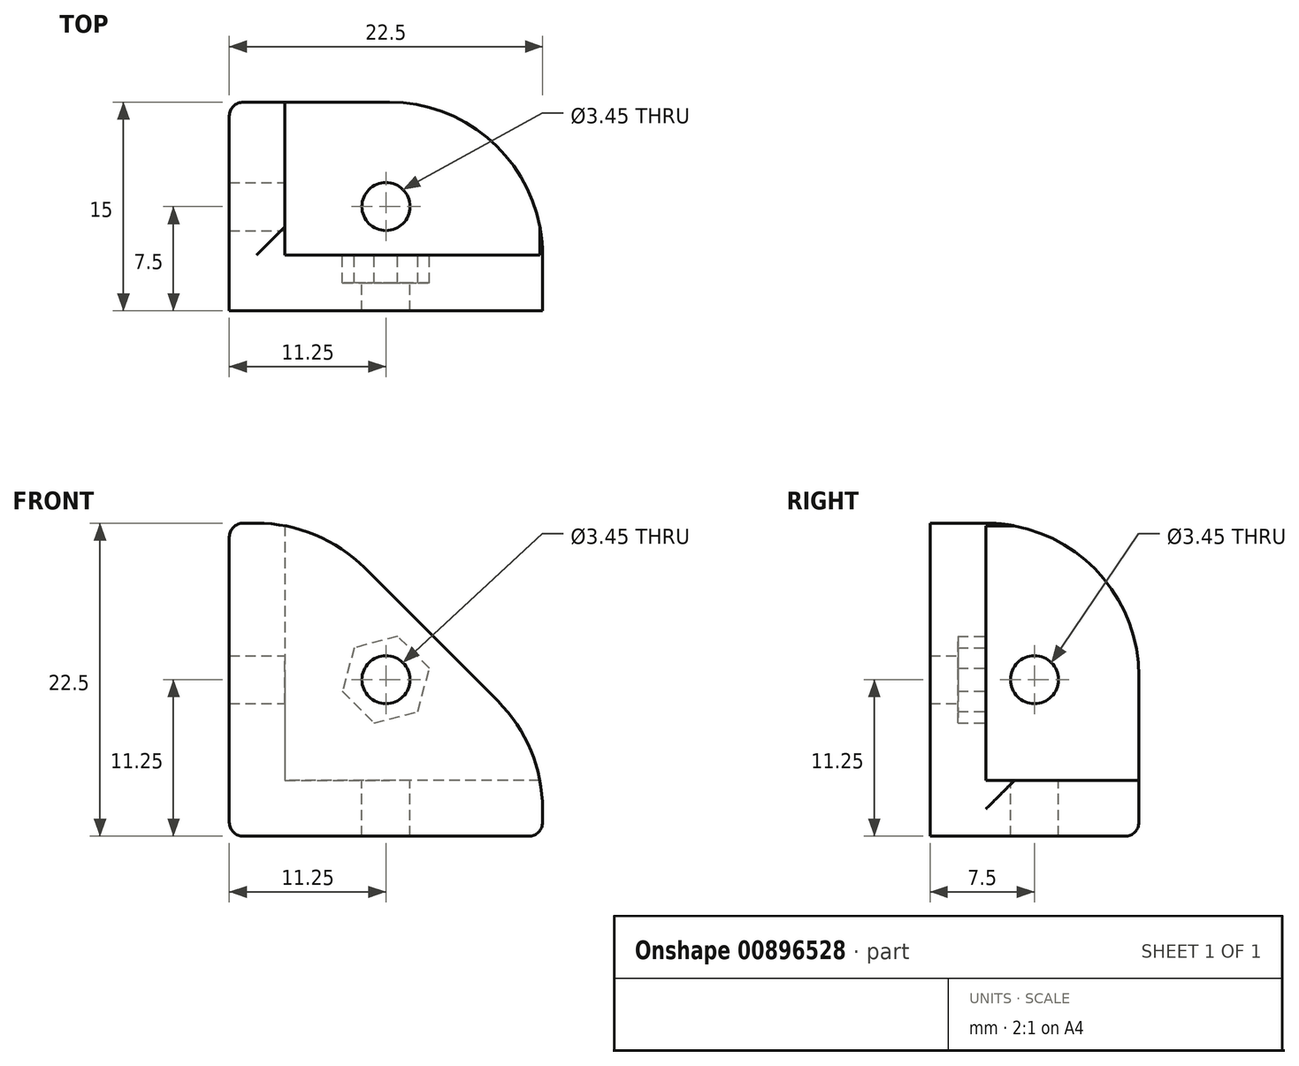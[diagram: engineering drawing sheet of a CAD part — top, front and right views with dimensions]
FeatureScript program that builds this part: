
annotation { "Feature Type Name" : "Feature", "Feature Type Description" : "" }
export const myFeature = defineFeature(function(context is Context, id is Id, definition is map)
    precondition{}
    {
        {
            assignVariable(context, id + "F0", {"variableType" : VariableType.LENGTH, "name" : "BeamWidth", "lengthValue" : 15 * mm});
        }
        {
            var Q0;
            Q0=qCreatedBy(makeId("Top.planeOp"),FACE);
            var sketch = newSketch(context, id + "F1", { "sketchPlane" : qUnion([Q0])});
            skLineSegment(sketch, "E0.bottom", {"start": v(0, 0) * mm, "end": v(22.5, 0) * mm});
            skLineSegment(sketch, "E0.top", {"start": v(0, 15) * mm, "end": v(22.5, 15) * mm});
            skLineSegment(sketch, "E0.left", {"start": v(0, 0) * mm, "end": v(0, 15) * mm});
            skLineSegment(sketch, "E0.right", {"start": v(22.5, 0) * mm, "end": v(22.5, 15) * mm});
            skSolve(sketch);
        }
        {
            var Q0;
            Q0 = qSketchRegion(id + "F1", true);
            extrude(context, id + "F2", {"entities" : qUnion([Q0]), "depth" : 4 * mm, "offsetDistance" : 25 * mm});
        }
        {
            var Q0;
            Q0=makeQuery(id+"F2.opExtrude","CAP_FACE",FACE,{"disambiguationData":[OSD([sQuery(id+"F1.wireOp",EDGE,"E0.bottom"),sQuery(id+"F1.wireOp",EDGE,"E0.top"),sQuery(id+"F1.wireOp",EDGE,"E0.left"),sQuery(id+"F1.wireOp",EDGE,"E0.right")])],"isStart":false});
            var sketch = newSketch(context, id + "F3", { "sketchPlane" : qUnion([Q0])});
            skLineSegment(sketch, "E1", {"start": v(0, 15) * mm, "end": v(0, 0) * mm});
            skLineSegment(sketch, "E2", {"start": v(0, 0) * mm, "end": v(22.5, 0) * mm});
            skLineSegment(sketch, "E3", {"start": v(22.5, 0) * mm, "end": v(22.5, 4) * mm});
            skLineSegment(sketch, "E4", {"start": v(22.5, 4) * mm, "end": v(4, 4) * mm});
            skLineSegment(sketch, "E5", {"start": v(4, 4) * mm, "end": v(4, 15) * mm});
            skLineSegment(sketch, "E6", {"start": v(4, 15) * mm, "end": v(0, 15) * mm});
            skSolve(sketch);
        }
        {
            var Q0;
            Q0 = qSketchRegion(id + "F3", true);
            extrude(context, id + "F4", {"entities" : qUnion([Q0]), "operationType" : NewBodyOperationType.ADD, "depth" : ((getVariable(context, 'BeamWidth') * 1.5) - 4 * mm), "offsetDistance" : 25 * mm});
        }
        {
            var Q0;
            Q0=makeQuery(id+"F2.opExtrude","CAP_FACE",FACE,{"disambiguationData":[OSD([sQuery(id+"F1.wireOp",EDGE,"E0.bottom"),sQuery(id+"F1.wireOp",EDGE,"E0.top"),sQuery(id+"F1.wireOp",EDGE,"E0.left"),sQuery(id+"F1.wireOp",EDGE,"E0.right")])],"isStart":false});
            var sketch = newSketch(context, id + "F5", { "sketchPlane" : qUnion([Q0])});
            skLineSegment(sketch, "E7.0", {"start": v(0, 0) * mm, "end": v(0, 15) * mm});
            skLineSegment(sketch, "E8.0", {"start": v(0, 0) * mm, "end": v(22.5, 0) * mm});
            skCircle(sketch, "E9", {"center": v(11.25, 7.5) * mm, "radius": 1.73 * mm});
            skLineSegment(sketch, "E10", {"start": v(0, 7.5) * mm, "end": v(11.25, 7.5) * mm, "construction": true});
            skLineSegment(sketch, "E11", {"start": v(11.25, 0) * mm, "end": v(11.25, 7.5) * mm, "construction": true});
            skCircle(sketch, "E12", {"center": v(11.25, 7.5) * mm, "radius": 3.5 * mm});
            skSolve(sketch);
        }
        {
            var Q0;
            Q0=makeQuery(id+"F5.imprint","IMPRINT",FACE,{"disambiguationData":[TD([[makeQuery(id+"F5.imprint","IMPRINT",EDGE,{"derivedFrom":sQuery(id+"F5.wireOp",EDGE,"E9")}),1.0]])]});
            extrude(context, id + "F6", {"entities" : qUnion([Q0]), "operationType" : NewBodyOperationType.REMOVE, "endBound" : BoundingType.UP_TO_NEXT, "oppositeDirection" : true, "depth" : 25 * mm, "offsetDistance" : 25 * mm});
        }
        {
            var Q0;
            Q0=makeQuery(id+"F4.opExtrude","SWEPT_FACE",FACE,{"disambiguationData":[OSD([sQuery(id+"F3.wireOp",EDGE,"E5")])]});
            var sketch = newSketch(context, id + "F7", { "sketchPlane" : qUnion([Q0])});
            skCircle(sketch, "E13", {"center": v(7.5, 11.25) * mm, "radius": 1.73 * mm});
            skLineSegment(sketch, "E14.0", {"start": v(0, 0) * mm, "end": v(15, 0) * mm});
            skLineSegment(sketch, "E15", {"start": v(7.5, 0) * mm, "end": v(7.5, 11.25) * mm, "construction": true});
            skLineSegment(sketch, "E16", {"start": v(0, 0) * mm, "end": v(0, 22.5) * mm, "construction": true});
            skLineSegment(sketch, "E17", {"start": v(7.5, 11.25) * mm, "end": v(0, 11.25) * mm, "construction": true});
            skCircle(sketch, "E18", {"center": v(7.5, 11.25) * mm, "radius": 3.5 * mm});
            skSolve(sketch);
        }
        {
            var Q0;
            Q0=makeQuery(id+"F7.imprint","IMPRINT",FACE,{"disambiguationData":[TD([[makeQuery(id+"F7.imprint","IMPRINT",EDGE,{"derivedFrom":sQuery(id+"F7.wireOp",EDGE,"E13")}),1.0]])]});
            extrude(context, id + "F8", {"entities" : qUnion([Q0]), "operationType" : NewBodyOperationType.REMOVE, "endBound" : BoundingType.UP_TO_NEXT, "oppositeDirection" : true, "depth" : 25 * mm, "offsetDistance" : 25 * mm});
        }
        {
            var Q0;
            Q0=makeQuery(id+"F4.opExtrude","SWEPT_FACE",FACE,{"disambiguationData":[OSD([sQuery(id+"F3.wireOp",EDGE,"E4")])]});
            var sketch = newSketch(context, id + "F9", { "sketchPlane" : qUnion([Q0])});
            skLineSegment(sketch, "E19.0", {"start": v(0, 0) * mm, "end": v(-22.5, 0) * mm});
            skLineSegment(sketch, "E20", {"start": v(0, 0) * mm, "end": v(0, 22.5) * mm, "construction": true});
            skCircle(sketch, "E21", {"center": v(-11.25, 11.25) * mm, "radius": 1.73 * mm});
            skLineSegment(sketch, "E22", {"start": v(-11.25, 11.25) * mm, "end": v(-11.25, 0) * mm, "construction": true});
            skLineSegment(sketch, "E23", {"start": v(-11.25, 11.25) * mm, "end": v(0, 11.25) * mm, "construction": true});
            skCircle(sketch, "E24.cCircle", {"center": v(-11.25, 11.25) * mm, "radius": 2.8 * mm, "construction": true});
            skLineSegment(sketch, "E24.0", {"start": v(-8.96, 13.54) * mm, "end": v(-8.13, 10.41) * mm});
            skLineSegment(sketch, "E24.1", {"start": v(-8.13, 10.41) * mm, "end": v(-10.41, 8.13) * mm});
            skLineSegment(sketch, "E24.2", {"start": v(-10.41, 8.13) * mm, "end": v(-13.54, 8.96) * mm});
            skLineSegment(sketch, "E24.3", {"start": v(-13.54, 8.96) * mm, "end": v(-14.37, 12.09) * mm});
            skLineSegment(sketch, "E24.4", {"start": v(-14.37, 12.09) * mm, "end": v(-12.09, 14.37) * mm});
            skLineSegment(sketch, "E24.5", {"start": v(-12.09, 14.37) * mm, "end": v(-8.96, 13.54) * mm});
            skPoint(sketch, "E24.0.midPoint", {"position": v(-8.55, 11.97) * mm});
            skSolve(sketch);
        }
        {
            var Q0;
            Q0=makeQuery(id+"F9.imprint","IMPRINT",FACE,{"disambiguationData":[TD([[makeQuery(id+"F9.imprint","IMPRINT",EDGE,{"derivedFrom":sQuery(id+"F9.wireOp",EDGE,"E21")}),1.0]])]});
            extrude(context, id + "F10", {"entities" : qUnion([Q0]), "operationType" : NewBodyOperationType.REMOVE, "endBound" : BoundingType.UP_TO_NEXT, "oppositeDirection" : true, "depth" : 25 * mm, "offsetDistance" : 25 * mm});
        }
        {
            var Q0;
            Q0 = qSketchRegion(id + "F9", true);
            extrude(context, id + "F11", {"entities" : qUnion([Q0]), "operationType" : NewBodyOperationType.REMOVE, "oppositeDirection" : true, "depth" : 2 * mm, "offsetDistance" : 25 * mm});
        }
        {
            var Q0;
            Q0=makeQuery(id+"F4.opExtrude","CAP_EDGE",EDGE,{"disambiguationData":[OSD([sQuery(id+"F3.wireOp",EDGE,"E3")])],"isStart":false});
            chamfer(context, id + "F12", {"entities" : qUnion([Q0]), "width" : 16 * mm, "tangentPropagation" : true});
        }
        {
            var Q0;
            Q0=makeQuery(id+"F2.opExtrude","SWEPT_EDGE",EDGE,{"disambiguationData":[OSD([sQuery(id+"F1.wireOp",EDGE,"E0.top"),sQuery(id+"F1.wireOp",EDGE,"E0.right")])]});
            var Q1;
            Q1=makeQuery(id+"F4.opExtrude","CAP_EDGE",EDGE,{"disambiguationData":[OSD([sQuery(id+"F3.wireOp",EDGE,"E6")])],"isStart":false});
            var Q2;
            {var subQ0=sQuery(id+"F3.wireOp",EDGE,"E3");Q2=makeQuery(id+"F12.opChamfer","BLEND_EDGE",EDGE,{"blendedFrom":[makeQuery(id+"F4.opExtrude","CAP_EDGE",EDGE,{"disambiguationData":[OSD([subQ0])],"isStart":false}),makeQuery(id+"F4.opExtrude","CAP_FACE",FACE,{"disambiguationData":[OSD([sQuery(id+"F3.wireOp",EDGE,"E1"),sQuery(id+"F3.wireOp",EDGE,"E2"),subQ0,sQuery(id+"F3.wireOp",EDGE,"E4"),sQuery(id+"F3.wireOp",EDGE,"E5"),sQuery(id+"F3.wireOp",EDGE,"E6")])],"isStart":false})],"blendedInto":[makeQuery(id+"F4.opExtrude","CAP_FACE",FACE,{"disambiguationData":[OSD([sQuery(id+"F3.wireOp",EDGE,"E1"),sQuery(id+"F3.wireOp",EDGE,"E2"),subQ0,sQuery(id+"F3.wireOp",EDGE,"E4"),sQuery(id+"F3.wireOp",EDGE,"E5"),sQuery(id+"F3.wireOp",EDGE,"E6")])],"isStart":false})]});}
            var Q3;
            {var subQ0=sQuery(id+"F3.wireOp",EDGE,"E3");Q3=makeQuery(id+"F12.opChamfer","BLEND_EDGE",EDGE,{"blendedFrom":[makeQuery(id+"F4.opExtrude","CAP_EDGE",EDGE,{"disambiguationData":[OSD([subQ0])],"isStart":false}),makeQuery(id+"F4.boolean.opBoolean","MERGE",FACE,{"derivedFrom":[makeQuery(id+"F2.opExtrude","SWEPT_FACE",FACE,{"disambiguationData":[OSD([sQuery(id+"F1.wireOp",EDGE,"E0.right")])]}),makeQuery(id+"F4.opExtrude","SWEPT_FACE",FACE,{"disambiguationData":[OSD([subQ0])]})]})],"blendedInto":[makeQuery(id+"F4.boolean.opBoolean","MERGE",FACE,{"derivedFrom":[makeQuery(id+"F2.opExtrude","SWEPT_FACE",FACE,{"disambiguationData":[OSD([sQuery(id+"F1.wireOp",EDGE,"E0.right")])]}),makeQuery(id+"F4.opExtrude","SWEPT_FACE",FACE,{"disambiguationData":[OSD([subQ0])]})]})]});}
            fillet(context, id + "F13", {"entities" : qUnion([Q0, Q1, Q2, Q3]), "radius" : 11 * mm, "tangentPropagation" : true, "allowEdgeOverflow" : false});
        }
        {
            var Q0;
            Q0=makeQuery(id+"F4.opExtrude","CAP_EDGE",EDGE,{"disambiguationData":[OSD([sQuery(id+"F3.wireOp",EDGE,"E1")])],"isStart":false});
            var Q1;
            Q1=makeQuery(id+"F2.opExtrude","CAP_EDGE",EDGE,{"disambiguationData":[OSD([sQuery(id+"F1.wireOp",EDGE,"E0.left")])],"isStart":true});
            var Q2;
            Q2=makeQuery(id+"F2.opExtrude","CAP_EDGE",EDGE,{"disambiguationData":[OSD([sQuery(id+"F1.wireOp",EDGE,"E0.right")])],"isStart":true});
            var Q3;
            Q3=makeQuery(id+"F4.opExtrude","CAP_EDGE",EDGE,{"disambiguationData":[OSD([sQuery(id+"F3.wireOp",EDGE,"E5")])],"isStart":true});
            fillet(context, id + "F14", {"entities" : qUnion([Q0, Q1, Q2, Q3]), "radius" : 1 * mm, "tangentPropagation" : true, "allowEdgeOverflow" : false});
        }
    });
